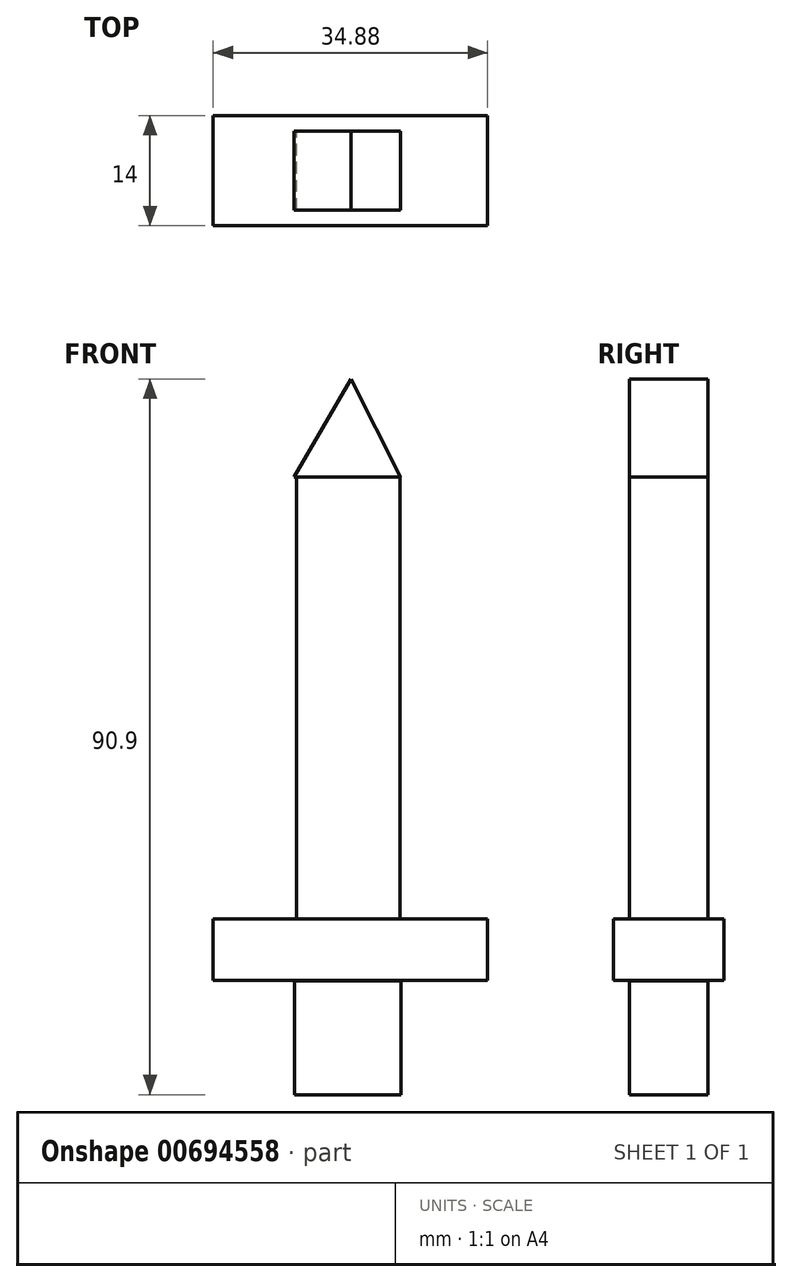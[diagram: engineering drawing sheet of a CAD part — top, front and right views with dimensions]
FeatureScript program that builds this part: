
annotation { "Feature Type Name" : "Feature", "Feature Type Description" : "" }
export const myFeature = defineFeature(function(context is Context, id is Id, definition is map)
    precondition{}
    {
        {
            var Q0;
            Q0=qCreatedBy(makeId("Front.planeOp"),FACE);
            var sketch = newSketch(context, id + "F0", { "sketchPlane" : qUnion([Q0])});
            skLineSegment(sketch, "E0", {"start": v(-30.85, 56.14) * mm, "end": v(-17.34, 56.14) * mm});
            skLineSegment(sketch, "E1", {"start": v(-17.34, 56.14) * mm, "end": v(-23.63, 68.57) * mm});
            skLineSegment(sketch, "E2", {"start": v(-23.63, 68.57) * mm, "end": v(-30.85, 56.14) * mm});
            skSolve(sketch);
        }
        {
            var Q0;
            Q0=qCreatedBy(makeId("Front.planeOp"),FACE);
            var sketch = newSketch(context, id + "F1", { "sketchPlane" : qUnion([Q0])});
            skLineSegment(sketch, "E3.bottom", {"start": v(-41.14, 0) * mm, "end": v(-6.26, 0) * mm});
            skLineSegment(sketch, "E3.top", {"start": v(-41.14, -7.81) * mm, "end": v(-6.26, -7.81) * mm});
            skLineSegment(sketch, "E3.left", {"start": v(-41.14, 0) * mm, "end": v(-41.14, -7.81) * mm});
            skLineSegment(sketch, "E3.right", {"start": v(-6.26, 0) * mm, "end": v(-6.26, -7.81) * mm});
            skSolve(sketch);
        }
        {
            var Q0;
            Q0=qCreatedBy(makeId("Front.planeOp"),FACE);
            var sketch = newSketch(context, id + "F2", { "sketchPlane" : qUnion([Q0])});
            skLineSegment(sketch, "E4.bottom", {"start": v(-30.78, -7.88) * mm, "end": v(-17.28, -7.88) * mm});
            skLineSegment(sketch, "E4.top", {"start": v(-30.78, -22.33) * mm, "end": v(-17.28, -22.33) * mm});
            skLineSegment(sketch, "E4.left", {"start": v(-30.78, -7.88) * mm, "end": v(-30.78, -22.33) * mm});
            skLineSegment(sketch, "E4.right", {"start": v(-17.28, -7.88) * mm, "end": v(-17.28, -22.33) * mm});
            skSolve(sketch);
        }
        {
            var Q0;
            Q0=makeQuery(id+"F0.imprint","IMPRINT",FACE,{"disambiguationData":[TD([[makeQuery(id+"F0.imprint","IMPRINT",EDGE,{"derivedFrom":sQuery(id+"F0.wireOp",EDGE,"E0")}),1.0]])]});
            var Q1;
            Q1=makeQuery(id+"Fd2zLwMToPuLOdr_0.imprint","IMPRINT",FACE,{"disambiguationData":[TD([[makeQuery(id+"Fd2zLwMToPuLOdr_0.imprint","IMPRINT",EDGE,{"derivedFrom":sQuery(id+"Fd2zLwMToPuLOdr_0.wireOp",EDGE,"lwPyYTaR-W7ix-wj9c-iSca-H4Xo3YnByWfR.bottom")}),1.0]])]});
            var Q2;
            Q2=makeQuery(id+"F2.imprint","IMPRINT",FACE,{"disambiguationData":[TD([[makeQuery(id+"F2.imprint","IMPRINT",EDGE,{"derivedFrom":sQuery(id+"F2.wireOp",EDGE,"E4.bottom")}),-1.0]])]});
            extrude(context, id + "F3", {"entities" : qUnion([Q0, Q1, Q2]), "depth" : 10 * mm, "offsetDistance" : 25.4 * mm});
        }
        {
            var Q0;
            Q0=makeQuery(id+"F1.imprint","IMPRINT",FACE,{"disambiguationData":[TD([[makeQuery(id+"F1.imprint","IMPRINT",EDGE,{"derivedFrom":sQuery(id+"F1.wireOp",EDGE,"E3.bottom")}),-1.0]])]});
            extrude(context, id + "F4", {"entities" : qUnion([Q0]), "depth" : 12 * mm, "offsetDistance" : 25.4 * mm});
        }
        {
            var Q0;
            Q0=makeQuery(id+"F4.opExtrude","CAP_FACE",FACE,{"disambiguationData":[OSD([sQuery(id+"F1.wireOp",EDGE,"E3.bottom"),sQuery(id+"F1.wireOp",EDGE,"E3.top"),sQuery(id+"F1.wireOp",EDGE,"E3.left"),sQuery(id+"F1.wireOp",EDGE,"E3.right")])],"isStart":true});
            extrude(context, id + "F5", {"entities" : qUnion([Q0]), "operationType" : NewBodyOperationType.ADD, "depth" : 2 * mm, "offsetDistance" : 25.4 * mm});
        }
        {
            var Q0;
            Q0=qCreatedBy(makeId("Front.planeOp"),FACE);
            var sketch = newSketch(context, id + "F6", { "sketchPlane" : qUnion([Q0])});
            skLineSegment(sketch, "E5.bottom", {"start": v(-30.54, 56.13) * mm, "end": v(-17.4, 56.13) * mm});
            skLineSegment(sketch, "E5.top", {"start": v(-30.54, 0) * mm, "end": v(-17.4, 0) * mm});
            skLineSegment(sketch, "E5.left", {"start": v(-30.54, 56.13) * mm, "end": v(-30.54, 0) * mm});
            skLineSegment(sketch, "E5.right", {"start": v(-17.4, 56.13) * mm, "end": v(-17.4, 0) * mm});
            skSolve(sketch);
        }
        {
            var Q0;
            Q0 = qSketchRegion(id + "F6", true);
            extrude(context, id + "F7", {"entities" : qUnion([Q0]), "operationType" : NewBodyOperationType.ADD, "depth" : 10 * mm, "offsetDistance" : 25.4 * mm});
        }
    });
